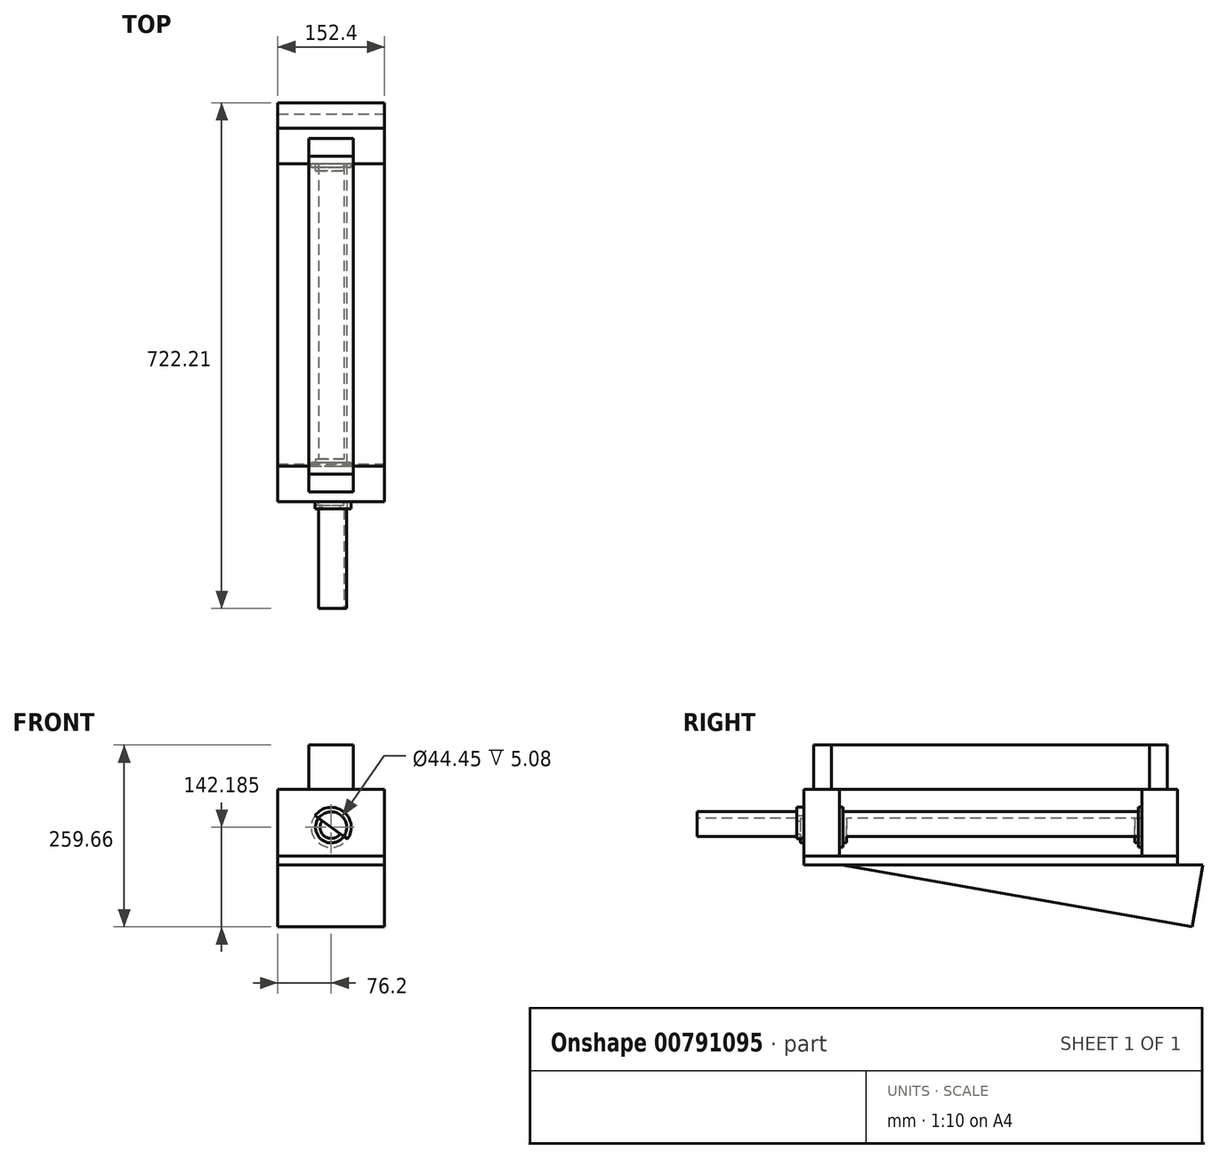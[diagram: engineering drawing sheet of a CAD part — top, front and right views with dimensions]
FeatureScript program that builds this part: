
annotation { "Feature Type Name" : "Feature", "Feature Type Description" : "" }
export const myFeature = defineFeature(function(context is Context, id is Id, definition is map)
    precondition{}
    {
        {
            var Q0;
            Q0=qCreatedBy(makeId("Top.planeOp"),FACE);
            var sketch = newSketch(context, id + "F0", { "sketchPlane" : qUnion([Q0])});
            skLineSegment(sketch, "E0.bottom", {"start": v(0, 0) * mm, "end": v(152.4, 0) * mm});
            skLineSegment(sketch, "E0.top", {"start": v(0, -533.4) * mm, "end": v(152.4, -533.4) * mm});
            skLineSegment(sketch, "E0.left", {"start": v(0, 0) * mm, "end": v(0, -533.4) * mm});
            skLineSegment(sketch, "E0.right", {"start": v(152.4, 0) * mm, "end": v(152.4, -533.4) * mm});
            skSolve(sketch);
        }
        {
            var Q0;
            Q0 = qSketchRegion(id + "F0", true);
            extrude(context, id + "F1", {"entities" : qUnion([Q0]), "depth" : 12.7 * mm, "offsetDistance" : 25.4 * mm});
        }
        {
            var Q0;
            Q0=makeQuery(id+"F1.opExtrude","CAP_FACE",FACE,{"disambiguationData":[OSD([sQuery(id+"F0.wireOp",EDGE,"E0.bottom"),sQuery(id+"F0.wireOp",EDGE,"E0.top"),sQuery(id+"F0.wireOp",EDGE,"E0.left"),sQuery(id+"F0.wireOp",EDGE,"E0.right")])],"isStart":false});
            var sketch = newSketch(context, id + "F2", { "sketchPlane" : qUnion([Q0])});
            skLineSegment(sketch, "E1", {"start": v(0, 0) * mm, "end": v(152.4, 0) * mm});
            skLineSegment(sketch, "E2", {"start": v(152.4, 0) * mm, "end": v(152.4, -50.8) * mm});
            skLineSegment(sketch, "E3", {"start": v(152.4, -50.8) * mm, "end": v(0, -50.8) * mm});
            skLineSegment(sketch, "E4", {"start": v(0, -50.8) * mm, "end": v(0, 0) * mm});
            skLineSegment(sketch, "E5", {"start": v(0, -533.4) * mm, "end": v(0, -482.6) * mm});
            skLineSegment(sketch, "E6", {"start": v(0, -482.6) * mm, "end": v(152.4, -482.6) * mm});
            skLineSegment(sketch, "E7", {"start": v(152.4, -482.6) * mm, "end": v(152.4, -533.4) * mm});
            skLineSegment(sketch, "E8", {"start": v(152.4, -533.4) * mm, "end": v(0, -533.4) * mm});
            skSolve(sketch);
        }
        {
            var Q0;
            Q0 = qSketchRegion(id + "F2", true);
            extrude(context, id + "F3", {"entities" : qUnion([Q0]), "depth" : 95.25 * mm, "offsetDistance" : 25.4 * mm});
        }
        {
            var Q0;
            Q0=makeQuery(id+"F3.opExtrude","CAP_FACE",FACE,{"disambiguationData":[OSD([sQuery(id+"F2.wireOp",EDGE,"E5"),sQuery(id+"F2.wireOp",EDGE,"E6"),sQuery(id+"F2.wireOp",EDGE,"E7"),sQuery(id+"F2.wireOp",EDGE,"E8")])],"isStart":false});
            var sketch = newSketch(context, id + "F4", { "sketchPlane" : qUnion([Q0])});
            skLineSegment(sketch, "E9", {"start": v(44.45, -519.11) * mm, "end": v(107.95, -519.11) * mm});
            skLineSegment(sketch, "E10", {"start": v(107.95, -519.11) * mm, "end": v(107.95, -493.71) * mm});
            skLineSegment(sketch, "E11", {"start": v(107.95, -493.71) * mm, "end": v(44.45, -493.71) * mm});
            skLineSegment(sketch, "E12", {"start": v(44.45, -493.71) * mm, "end": v(44.45, -519.11) * mm});
            skLineSegment(sketch, "E13.bottom", {"start": v(44.45, -14.29) * mm, "end": v(107.95, -14.29) * mm});
            skLineSegment(sketch, "E13.top", {"start": v(44.45, -39.69) * mm, "end": v(107.95, -39.69) * mm});
            skLineSegment(sketch, "E13.left", {"start": v(44.45, -14.29) * mm, "end": v(44.45, -39.69) * mm});
            skLineSegment(sketch, "E13.right", {"start": v(107.95, -14.29) * mm, "end": v(107.95, -39.69) * mm});
            skSolve(sketch);
        }
        {
            var Q0;
            Q0 = qSketchRegion(id + "F4", true);
            extrude(context, id + "F5", {"entities" : qUnion([Q0]), "depth" : 63.5 * mm, "offsetDistance" : 25.4 * mm});
        }
        {
            var Q0;
            Q0=makeQuery(id+"F3.boolean.opBoolean","MERGE",FACE,{"derivedFrom":[makeQuery(id+"F1.opExtrude","SWEPT_FACE",FACE,{"disambiguationData":[OSD([sQuery(id+"F0.wireOp",EDGE,"E0.top")])]}),makeQuery(id+"F3.opExtrude","SWEPT_FACE",FACE,{"disambiguationData":[OSD([sQuery(id+"F2.wireOp",EDGE,"E8")])]})]});
            var sketch = newSketch(context, id + "F6", { "sketchPlane" : qUnion([Q0])});
            skLineSegment(sketch, "E14", {"start": v(0, 0) * mm, "end": v(152.4, 107.95) * mm});
            skLineSegment(sketch, "E15", {"start": v(0, 107.95) * mm, "end": v(152.4, 0) * mm});
            skCircle(sketch, "E16", {"center": v(76.2, 53.98) * mm, "radius": 15.88 * mm});
            skCircle(sketch, "E17", {"center": v(76.2, 53.98) * mm, "radius": 22.23 * mm});
            skCircle(sketch, "E18", {"center": v(76.2, 53.98) * mm, "radius": 28.58 * mm});
            skSolve(sketch);
        }
        {
            var Q0;
            {var subQ0=sQuery(id+"F6.wireOp",EDGE,"E16");var subQ1=sQuery(id+"F6.wireOp",EDGE,"E14");var subQ2=makeQuery(id+"F6.imprint","INTERSECT",VERTEX,{"disambiguationData":[OD(0.0)],"derivedFrom":[subQ1,subQ0]});Q0=makeQuery(id+"F6.imprint","IMPRINT",FACE,{"disambiguationData":[TD([[makeQuery(id+"F6.imprint","IMPRINT",EDGE,{"disambiguationData":[TD([[subQ2,-1.0]])],"derivedFrom":subQ1}),1.0]])]});}
            var Q1;
            {var subQ0=sQuery(id+"F6.wireOp",EDGE,"E16");var subQ1=sQuery(id+"F6.wireOp",EDGE,"E14");var subQ2=makeQuery(id+"F6.imprint","INTERSECT",VERTEX,{"disambiguationData":[OD(0.0)],"derivedFrom":[subQ1,subQ0]});Q1=makeQuery(id+"F6.imprint","IMPRINT",FACE,{"disambiguationData":[TD([[makeQuery(id+"F6.imprint","IMPRINT",EDGE,{"disambiguationData":[TD([[subQ2,-1.0]])],"derivedFrom":subQ1}),-1.0]])]});}
            var Q2;
            {var subQ0=sQuery(id+"F6.wireOp",EDGE,"E15");var subQ1=sQuery(id+"F6.wireOp",EDGE,"E14");var subQ2=makeQuery(id+"F6.imprint","INTERSECT",VERTEX,{"derivedFrom":[subQ1,subQ0]});Q2=makeQuery(id+"F6.imprint","IMPRINT",FACE,{"disambiguationData":[TD([[makeQuery(id+"F6.imprint","IMPRINT",EDGE,{"disambiguationData":[TD([[subQ2,-1.0]])],"derivedFrom":subQ1}),1.0]])]});}
            var Q3;
            {var subQ0=sQuery(id+"F6.wireOp",EDGE,"E15");var subQ1=sQuery(id+"F6.wireOp",EDGE,"E14");var subQ2=makeQuery(id+"F6.imprint","INTERSECT",VERTEX,{"derivedFrom":[subQ1,subQ0]});Q3=makeQuery(id+"F6.imprint","IMPRINT",FACE,{"disambiguationData":[TD([[makeQuery(id+"F6.imprint","IMPRINT",EDGE,{"disambiguationData":[TD([[subQ2,-1.0]])],"derivedFrom":subQ1}),-1.0]])]});}
            var Q4;
            Q4=makeQuery(id+"F3.opExtrude","SWEPT_FACE",FACE,{"disambiguationData":[OSD([sQuery(id+"F2.wireOp",EDGE,"E3")])]});
            extrude(context, id + "F7", {"entities" : qUnion([Q0, Q1, Q2, Q3]), "operationType" : NewBodyOperationType.ADD, "endBound" : BoundingType.UP_TO_SURFACE, "oppositeDirection" : true, "depth" : 25.4 * mm, "endBoundEntityFace" : qUnion([Q4]), "offsetDistance" : 25.4 * mm, "hasSecondDirection" : true, "secondDirectionOppositeDirection" : false, "secondDirectionDepth" : 152.4 * mm});
        }
        {
            var Q0;
            Q0=makeQuery(id+"F3.opExtrude","SWEPT_FACE",FACE,{"disambiguationData":[OSD([sQuery(id+"F2.wireOp",EDGE,"E3")])]});
            var sketch = newSketch(context, id + "F8", { "sketchPlane" : qUnion([Q0])});
            skCircle(sketch, "E19", {"center": v(76.2, 53.98) * mm, "radius": 22.23 * mm});
            skCircle(sketch, "E20", {"center": v(76.2, 53.98) * mm, "radius": 28.58 * mm});
            skSolve(sketch);
        }
        {
            var Q0;
            Q0=makeQuery(id+"F8.imprint","IMPRINT",FACE,{"disambiguationData":[TD([[makeQuery(id+"F8.imprint","IMPRINT",EDGE,{"derivedFrom":sQuery(id+"F8.wireOp",EDGE,"E19")}),1.0]])]});
            extrude(context, id + "F9", {"entities" : qUnion([Q0]), "depth" : 10.16 * mm, "offsetDistance" : 25.4 * mm});
        }
        {
            var Q0;
            Q0 = qSketchRegion(id + "F8", true);
            extrude(context, id + "F10", {"entities" : qUnion([Q0]), "depth" : 5.08 * mm, "offsetDistance" : 25.4 * mm});
        }
        {
            var Q0;
            {var subQ0=sQuery(id+"F6.wireOp",EDGE,"E17");var subQ1=sQuery(id+"F6.wireOp",EDGE,"E14");var subQ2=makeQuery(id+"F6.imprint","INTERSECT",VERTEX,{"disambiguationData":[OD(0.0)],"derivedFrom":[subQ1,subQ0]});Q0=makeQuery(id+"F6.imprint","IMPRINT",FACE,{"disambiguationData":[TD([[makeQuery(id+"F6.imprint","IMPRINT",EDGE,{"disambiguationData":[TD([[subQ2,-1.0]])],"derivedFrom":subQ1}),-1.0]])]});}
            var Q1;
            {var subQ0=sQuery(id+"F6.wireOp",EDGE,"E17");var subQ1=sQuery(id+"F6.wireOp",EDGE,"E14");var subQ2=makeQuery(id+"F6.imprint","INTERSECT",VERTEX,{"disambiguationData":[OD(0.0)],"derivedFrom":[subQ1,subQ0]});Q1=makeQuery(id+"F6.imprint","IMPRINT",FACE,{"disambiguationData":[TD([[makeQuery(id+"F6.imprint","IMPRINT",EDGE,{"disambiguationData":[TD([[subQ2,-1.0]])],"derivedFrom":subQ1}),1.0]])]});}
            var Q2;
            {var subQ0=sQuery(id+"F6.wireOp",EDGE,"E16");var subQ1=sQuery(id+"F6.wireOp",EDGE,"E14");var subQ2=makeQuery(id+"F6.imprint","INTERSECT",VERTEX,{"disambiguationData":[OD(1.0)],"derivedFrom":[subQ1,subQ0]});Q2=makeQuery(id+"F6.imprint","IMPRINT",FACE,{"disambiguationData":[TD([[makeQuery(id+"F6.imprint","IMPRINT",EDGE,{"disambiguationData":[TD([[subQ2,-1.0]])],"derivedFrom":subQ1}),1.0]])]});}
            var Q3;
            {var subQ0=sQuery(id+"F6.wireOp",EDGE,"E16");var subQ1=sQuery(id+"F6.wireOp",EDGE,"E14");var subQ2=makeQuery(id+"F6.imprint","INTERSECT",VERTEX,{"disambiguationData":[OD(1.0)],"derivedFrom":[subQ1,subQ0]});Q3=makeQuery(id+"F6.imprint","IMPRINT",FACE,{"disambiguationData":[TD([[makeQuery(id+"F6.imprint","IMPRINT",EDGE,{"disambiguationData":[TD([[subQ2,-1.0]])],"derivedFrom":subQ1}),-1.0]])]});}
            extrude(context, id + "F11", {"entities" : qUnion([Q0, Q1, Q2, Q3]), "operationType" : NewBodyOperationType.ADD, "depth" : 10.16 * mm, "offsetDistance" : 25.4 * mm});
        }
        {
            var Q0;
            {var subQ0=sQuery(id+"F6.wireOp",EDGE,"E17");var subQ1=sQuery(id+"F6.wireOp",EDGE,"E14");var subQ2=makeQuery(id+"F6.imprint","INTERSECT",VERTEX,{"disambiguationData":[OD(1.0)],"derivedFrom":[subQ1,subQ0]});Q0=makeQuery(id+"F6.imprint","IMPRINT",FACE,{"disambiguationData":[TD([[makeQuery(id+"F6.imprint","IMPRINT",EDGE,{"disambiguationData":[TD([[subQ2,-1.0]])],"derivedFrom":subQ1}),1.0]])]});}
            var Q1;
            {var subQ0=sQuery(id+"F6.wireOp",EDGE,"E18");var subQ1=sQuery(id+"F6.wireOp",EDGE,"E14");var subQ2=makeQuery(id+"F6.imprint","INTERSECT",VERTEX,{"disambiguationData":[OD(0.0)],"derivedFrom":[subQ1,subQ0]});Q1=makeQuery(id+"F6.imprint","IMPRINT",FACE,{"disambiguationData":[TD([[makeQuery(id+"F6.imprint","IMPRINT",EDGE,{"disambiguationData":[TD([[subQ2,-1.0]])],"derivedFrom":subQ1}),1.0]])]});}
            var Q2;
            {var subQ0=sQuery(id+"F6.wireOp",EDGE,"E18");var subQ1=sQuery(id+"F6.wireOp",EDGE,"E14");var subQ2=makeQuery(id+"F6.imprint","INTERSECT",VERTEX,{"disambiguationData":[OD(0.0)],"derivedFrom":[subQ1,subQ0]});Q2=makeQuery(id+"F6.imprint","IMPRINT",FACE,{"disambiguationData":[TD([[makeQuery(id+"F6.imprint","IMPRINT",EDGE,{"disambiguationData":[TD([[subQ2,-1.0]])],"derivedFrom":subQ1}),-1.0]])]});}
            var Q3;
            {var subQ0=sQuery(id+"F6.wireOp",EDGE,"E17");var subQ1=sQuery(id+"F6.wireOp",EDGE,"E14");var subQ2=makeQuery(id+"F6.imprint","INTERSECT",VERTEX,{"disambiguationData":[OD(1.0)],"derivedFrom":[subQ1,subQ0]});Q3=makeQuery(id+"F6.imprint","IMPRINT",FACE,{"disambiguationData":[TD([[makeQuery(id+"F6.imprint","IMPRINT",EDGE,{"disambiguationData":[TD([[subQ2,-1.0]])],"derivedFrom":subQ1}),-1.0]])]});}
            extrude(context, id + "F12", {"entities" : qUnion([Q0, Q1, Q2, Q3]), "operationType" : NewBodyOperationType.ADD, "depth" : 5.08 * mm, "offsetDistance" : 25.4 * mm});
        }
        {
            var Q0;
            Q0=makeQuery(id+"F3.opExtrude","SWEPT_FACE",FACE,{"disambiguationData":[OSD([sQuery(id+"F2.wireOp",EDGE,"E6")])]});
            var sketch = newSketch(context, id + "F13", { "sketchPlane" : qUnion([Q0])});
            skCircle(sketch, "E21", {"center": v(-76.2, 53.98) * mm, "radius": 22.23 * mm});
            skCircle(sketch, "E22", {"center": v(-76.2, 53.98) * mm, "radius": 28.58 * mm});
            skSolve(sketch);
        }
        {
            var Q0;
            Q0=makeQuery(id+"F13.imprint","IMPRINT",FACE,{"disambiguationData":[TD([[makeQuery(id+"F13.imprint","IMPRINT",EDGE,{"derivedFrom":sQuery(id+"F13.wireOp",EDGE,"E21")}),1.0]])]});
            extrude(context, id + "F14", {"entities" : qUnion([Q0]), "operationType" : NewBodyOperationType.ADD, "depth" : 10.16 * mm, "offsetDistance" : 25.4 * mm});
        }
        {
            var Q0;
            Q0 = qSketchRegion(id + "F13", true);
            extrude(context, id + "F15", {"entities" : qUnion([Q0]), "operationType" : NewBodyOperationType.ADD, "depth" : 5.08 * mm, "offsetDistance" : 25.4 * mm});
        }
        {
            var Q0;
            Q0=makeQuery(id+"F5.opExtrude","SWEPT_FACE",FACE,{"disambiguationData":[OSD([sQuery(id+"F4.wireOp",EDGE,"E11")])]});
            var Q1;
            Q1=makeQuery(id+"F5.opExtrude","SWEPT_FACE",FACE,{"disambiguationData":[OSD([sQuery(id+"F4.wireOp",EDGE,"E13.top")])]});
            extrude(context, id + "F16", {"entities" : qUnion([Q0]), "endBound" : BoundingType.UP_TO_SURFACE, "depth" : 482.6 * mm, "endBoundEntityFace" : qUnion([Q1]), "offsetDistance" : 25.4 * mm});
        }
        {
            var Q0;
            Q0=makeQuery(id+"F1.opExtrude","SWEPT_FACE",FACE,{"disambiguationData":[OSD([sQuery(id+"F0.wireOp",EDGE,"E0.right")])]});
            var sketch = newSketch(context, id + "F17", { "sketchPlane" : qUnion([Q0])});
            skLineSegment(sketch, "E23", {"start": v(-533.4, 0) * mm, "end": v(-479.43, 0) * mm});
            skLineSegment(sketch, "E24", {"start": v(-479.43, 0) * mm, "end": v(20.86, -88.21) * mm});
            skLineSegment(sketch, "E25", {"start": v(20.86, -88.21) * mm, "end": v(36.41, 0) * mm});
            skLineSegment(sketch, "E26", {"start": v(-479.43, 0) * mm, "end": v(36.41, 0) * mm});
            skSolve(sketch);
        }
        {
            var Q0;
            {var subQ0=sQuery(id+"F17.wireOp",EDGE,"E24");Q0=makeQuery(id+"F17.imprint","IMPRINT",FACE,{"disambiguationData":[TD([[makeQuery(id+"F17.imprint","IMPRINT",EDGE,{"derivedFrom":subQ0}),1.0]])]});}
            extrude(context, id + "F18", {"entities" : qUnion([Q0]), "oppositeDirection" : true, "depth" : 152.4 * mm, "offsetDistance" : 25.4 * mm});
        }
    });
